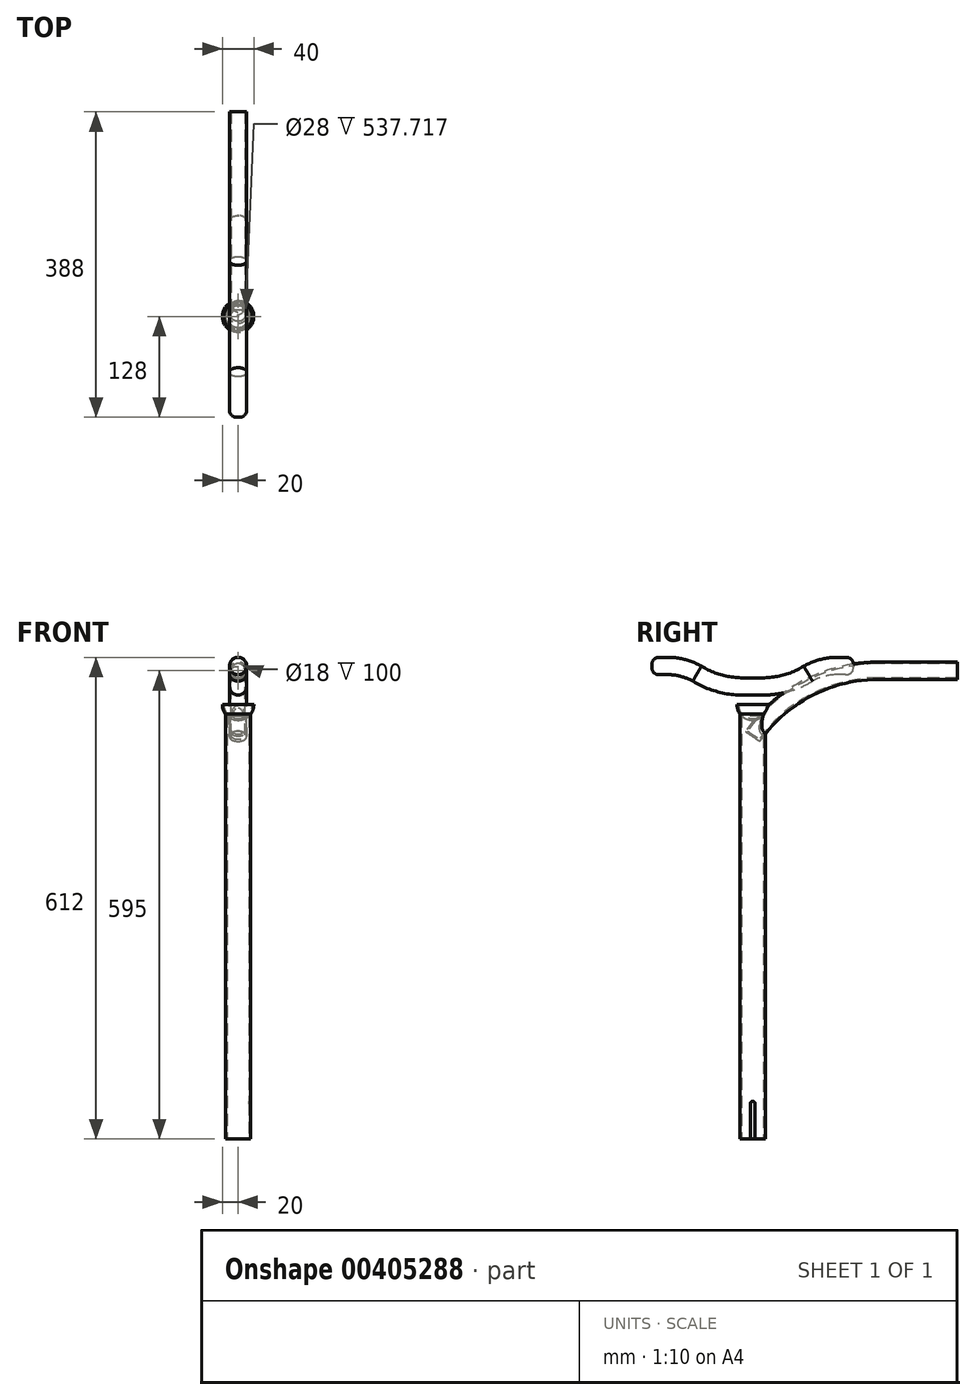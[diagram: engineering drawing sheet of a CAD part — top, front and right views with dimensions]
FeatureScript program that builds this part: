
annotation { "Feature Type Name" : "Feature", "Feature Type Description" : "" }
export const myFeature = defineFeature(function(context is Context, id is Id, definition is map)
    precondition{}
    {
        {
            var Q0;
            Q0=qCreatedBy(makeId("Top.planeOp"),FACE);
            var sketch = newSketch(context, id + "F0", { "sketchPlane" : qUnion([Q0])});
            skCircle(sketch, "E0", {"center": v(0, 0) * mm, "radius": 16 * mm});
            skSolve(sketch);
        }
        {
            var Q0;
            Q0=makeQuery(id+"F0.imprint","IMPRINT",FACE,{"disambiguationData":[TD([[makeQuery(id+"F0.imprint","IMPRINT",EDGE,{"derivedFrom":sQuery(id+"F0.wireOp",EDGE,"E0")}),1.0]])]});
            extrude(context, id + "F1", {"entities" : qUnion([Q0]), "depth" : 550 * mm});
        }
        {
            var Q0;
            Q0=makeQuery(id+"F1.opExtrude","CAP_FACE",FACE,{"disambiguationData":[OSD([sQuery(id+"F0.wireOp",EDGE,"E0")])],"isStart":true});
            shell(context, id + "F2", {"entities" : qUnion([Q0]), "thickness" : 2 * mm});
        }
        {
            var Q0;
            Q0=qCreatedBy(makeId("Right.planeOp"),FACE);
            var sketch = newSketch(context, id + "F3", { "sketchPlane" : qUnion([Q0])});
            skLineSegment(sketch, "E1.bottom", {"start": v(-3, 0) * mm, "end": v(3, 0) * mm});
            skLineSegment(sketch, "E1.left", {"start": v(-3, 0) * mm, "end": v(-3, 45) * mm});
            skLineSegment(sketch, "E1.right", {"start": v(3, 0) * mm, "end": v(3, 45) * mm});
            skArc(sketch, "E2", {"start": v(3, 45) * mm, "mid": v(0, 48) * mm, "end": v(-3, 45) * mm});
            skSolve(sketch);
        }
        {
            var Q0;
            Q0 = qSketchRegion(id + "F3", true);
            extrude(context, id + "F4", {"entities" : qUnion([Q0]), "operationType" : NewBodyOperationType.REMOVE, "endBound" : BoundingType.THROUGH_ALL, "depth" : 25 * mm});
        }
        {
            var Q0;
            Q0=qCreatedBy(makeId("Right.planeOp"),FACE);
            var sketch = newSketch(context, id + "F5", { "sketchPlane" : qUnion([Q0])});
            skArc(sketch, "E3", {"start": v(160, 595) * mm, "mid": v(69.75, 572.86) * mm, "end": v(0, 511.47) * mm});
            skLineSegment(sketch, "E4", {"start": v(160, 595) * mm, "end": v(260, 595) * mm});
            skSolve(sketch);
        }
        {
            var Q0;
            Q0=sQuery(id+"F5.wireOp",VERTEX,"E4.end");
            var Q1;
            Q1=qCreatedBy(makeId("Front.planeOp"),FACE);
            cPlane(context, id + "F6", {"entities" : qUnion([Q0, Q1]), "cplaneType" : CPlaneType.PLANE_POINT, "offset" : 25 * mm, "width" : 150 * mm, "height" : 150 * mm});
        }
        {
            var Q0;
            Q0=qCreatedBy(id+"F6.planeOp",FACE);
            var sketch = newSketch(context, id + "F7", { "sketchPlane" : qUnion([Q0])});
            skCircle(sketch, "E5", {"center": v(0, 595) * mm, "radius": 11 * mm});
            skSolve(sketch);
        }
        {
            var Q0;
            Q0=makeQuery(id+"F7.imprint","IMPRINT",FACE,{"disambiguationData":[TD([[makeQuery(id+"F7.imprint","IMPRINT",EDGE,{"derivedFrom":sQuery(id+"F7.wireOp",EDGE,"E5")}),1.0]])]});
            var Q1;
            Q1 = qConstructionFilter(qBodyType(qCreatedBy(id + "F5" ,EDGE), BodyType.WIRE), ConstructionObject.NO);
            sweep(context, id + "F8", {"operationType" : NewBodyOperationType.ADD, "profiles" : qUnion([Q0]), "path" : qUnion([Q1])});
        }
        {
            var Q0;
            Q0=makeQuery(id+"F8.opSweep","CAP_FACE",FACE,{"disambiguationData":[OSD([sQuery(id+"F5.wireOp",VERTEX,"E4.end"),sQuery(id+"F7.wireOp",EDGE,"E5")])],"isStart":true});
            shell(context, id + "F9", {"entities" : qUnion([Q0]), "thickness" : 2 * mm});
        }
        {
            var Q0;
            Q0=qCreatedBy(makeId("Right.planeOp"),FACE);
            var sketch = newSketch(context, id + "F10", { "sketchPlane" : qUnion([Q0])});
            skLineSegment(sketch, "E6", {"start": v(-128, 601) * mm, "end": v(-108, 601) * mm});
            skArc(sketch, "E7", {"start": v(-70.5, 591.19) * mm, "mid": v(-88.62, 598.5) * mm, "end": v(-108, 601) * mm});
            skArc(sketch, "E8", {"start": v(-70.5, 591.19) * mm, "mid": v(-42.6, 579.12) * mm, "end": v(-12.5, 575) * mm});
            skLineSegment(sketch, "E9", {"start": v(-12.5, 575) * mm, "end": v(0, 575) * mm});
            skLineSegment(sketch, "E10", {"start": v(0, 0) * mm, "end": v(0, 575) * mm, "construction": true});
            skArc(sketch, "E11.MirrorCS", {"start": v(70.5, 591.19) * mm, "mid": v(42.6, 579.12) * mm, "end": v(12.5, 575) * mm});
            skLineSegment(sketch, "E12.MirrorCS", {"start": v(12.5, 575) * mm, "end": v(0, 575) * mm});
            skArc(sketch, "E13.MirrorCS", {"start": v(70.5, 591.19) * mm, "mid": v(88.62, 598.5) * mm, "end": v(108, 601) * mm});
            skLineSegment(sketch, "E14.MirrorCS", {"start": v(128, 601) * mm, "end": v(108, 601) * mm});
            skSolve(sketch);
        }
        {
            var Q0;
            Q0=sQuery(id+"F10.wireOp",VERTEX,"E14.MirrorCS.start");
            var Q1;
            Q1=qCreatedBy(id+"F6.planeOp",FACE);
            cPlane(context, id + "F11", {"entities" : qUnion([Q0, Q1]), "cplaneType" : CPlaneType.PLANE_POINT, "offset" : 25 * mm, "width" : 150 * mm, "height" : 150 * mm});
        }
        {
            var Q0;
            Q0=qCreatedBy(id+"F11.planeOp",FACE);
            var sketch = newSketch(context, id + "F12", { "sketchPlane" : qUnion([Q0])});
            skCircle(sketch, "E15", {"center": v(0, 601) * mm, "radius": 11 * mm});
            skSolve(sketch);
        }
        {
            var Q0;
            Q0 = qSketchRegion(id + "F12", true);
            var Q1;
            Q1 = qConstructionFilter(qBodyType(qCreatedBy(id + "F10" ,EDGE), BodyType.WIRE), ConstructionObject.NO);
            sweep(context, id + "F13", {"profiles" : qUnion([Q0]), "path" : qUnion([Q1])});
        }
        {
            var Q0;
            Q0=makeQuery(id+"F13.opSweep","CAP_EDGE",EDGE,{"disambiguationData":[OSD([sQuery(id+"F10.wireOp",VERTEX,"E6.start"),sQuery(id+"F12.wireOp",EDGE,"E15")])],"isStart":false});
            var Q1;
            Q1=makeQuery(id+"F13.opSweep","CAP_EDGE",EDGE,{"disambiguationData":[OSD([sQuery(id+"F10.wireOp",VERTEX,"E14.MirrorCS.start"),sQuery(id+"F12.wireOp",EDGE,"E15")])],"isStart":true});
            fillet(context, id + "F14", {"entities" : qUnion([Q0, Q1]), "radius" : 10 * mm, "tangentPropagation" : true, "rho" : .5, "crossSection" : FilletCrossSection.CONIC, "allowEdgeOverflow" : false});
        }
        {
            var Q0;
            Q0=qCreatedBy(makeId("Right.planeOp"),FACE);
            var sketch = newSketch(context, id + "F15", { "sketchPlane" : qUnion([Q0])});
            skArc(sketch, "E16", {"start": v(-20, 551.93) * mm, "mid": v(-14.12, 537.83) * mm, "end": v(0, 532) * mm});
            skLineSegment(sketch, "E17", {"start": v(0, 532) * mm, "end": v(0, 552) * mm});
            skLineSegment(sketch, "E18", {"start": v(-20, 551.93) * mm, "end": v(0, 551.93) * mm});
            skPoint(sketch, "E19.orphan", {"position": v(0, 529.24) * mm});
            skSolve(sketch);
        }
        {
            var Q0;
            Q0 = qSketchRegion(id + "F15", true);
            var Q1;
            Q1=sQuery(id+"F15.wireOp",EDGE,"E17");
            revolve(context, id + "F16", {"operationType" : NewBodyOperationType.ADD, "entities" : qUnion([Q0]), "axis" : qUnion([Q1]), "revolveType" : RevolveType.FULL});
        }
        {
            var Q0;
            Q0=makeQuery(id+"F16.opRevolve","SWEPT_FACE",FACE,{"disambiguationData":[OSD([sQuery(id+"F15.wireOp",EDGE,"E18")])]});
            shell(context, id + "F17", {"entities" : qUnion([Q0]), "thickness" : 2 * mm});
        }
    });
